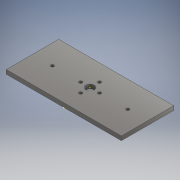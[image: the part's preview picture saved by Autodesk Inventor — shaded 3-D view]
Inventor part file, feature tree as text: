
AUTODESK INVENTOR PART (.ipt)
format: ipt  version: 2018 (Build 220112000, 112)  size: 121,344 bytes
history: native  units: mm
features: sketch x3, other x1, extrude x1
ambient origin geometry x8: Origin, YZ Plane, XZ Plane, XY Plane, X Axis, Y Axis, Z Axis, Center Point
bodies: Body1 (feature_tree)
feature tree (5):
  other  "Sólido1"
  extrude  "Extrusión1"  Depth=25.0mm
  sketch  "Boceto2"  dims[d2=4.0mm]
  sketch  "Boceto3"  dims[d4=1.5mm d8=1.5mm d9=1.5mm d10=1.5mm d15=1.5mm d16=1.5mm d17=2.0mm d18=0.0mm]
  sketch  "Boceto1"  dims[d0=55.0mm d1=25.0mm]
